# Revit family: QF_ELECTROLUXPROFESSIONAL_206447_E9SSEEAOMAE
name_source: partatom
category: Attrezzature speciali
units: mm (PartAtom-declared; Revit-internal decimal feet)

## family parameters
Attiva taglio nelle viste = No
Basato su piano di lavoro = No
Condiviso = No
Mantieni orientamento annotazione = No
Punto di calcolo locali = No
Quota connettore circolare = Usa diametro
Sempre verticale = Sì
Taglio con vuoti quando caricato = No
Tipo di parte = Normale

## types (1)
- QF_ELECTROLUXPROFESSIONAL_206447_E9SSEEAOMAE
    Descrizione = 900XP 4 GAS BURNERS 6kW ON GAS OVEN
    Direct Waste Size = 0"
    Gas Connection Height = 0 mm  [stored 0 ft]
    Gas Size = 1"
    HP = 0 HP
    Modello = 391005
    Produttore = ELECTROLUX
    Prospetto di default = 0 mm  [stored 0 ft]
    URL = www.electrolux.com
    URL Cutsheet = www.electrolux.com
    Watts = 0 W
    Weight in Pounds = 115

note: [stored X ft] marks values corroborated as IEEE doubles in the binary element streams (Revit-internal decimal feet)

## geometry (parser evidence)
native form markers: Blend x12, Sweep x1
no freeform markers — native parametric forms only
